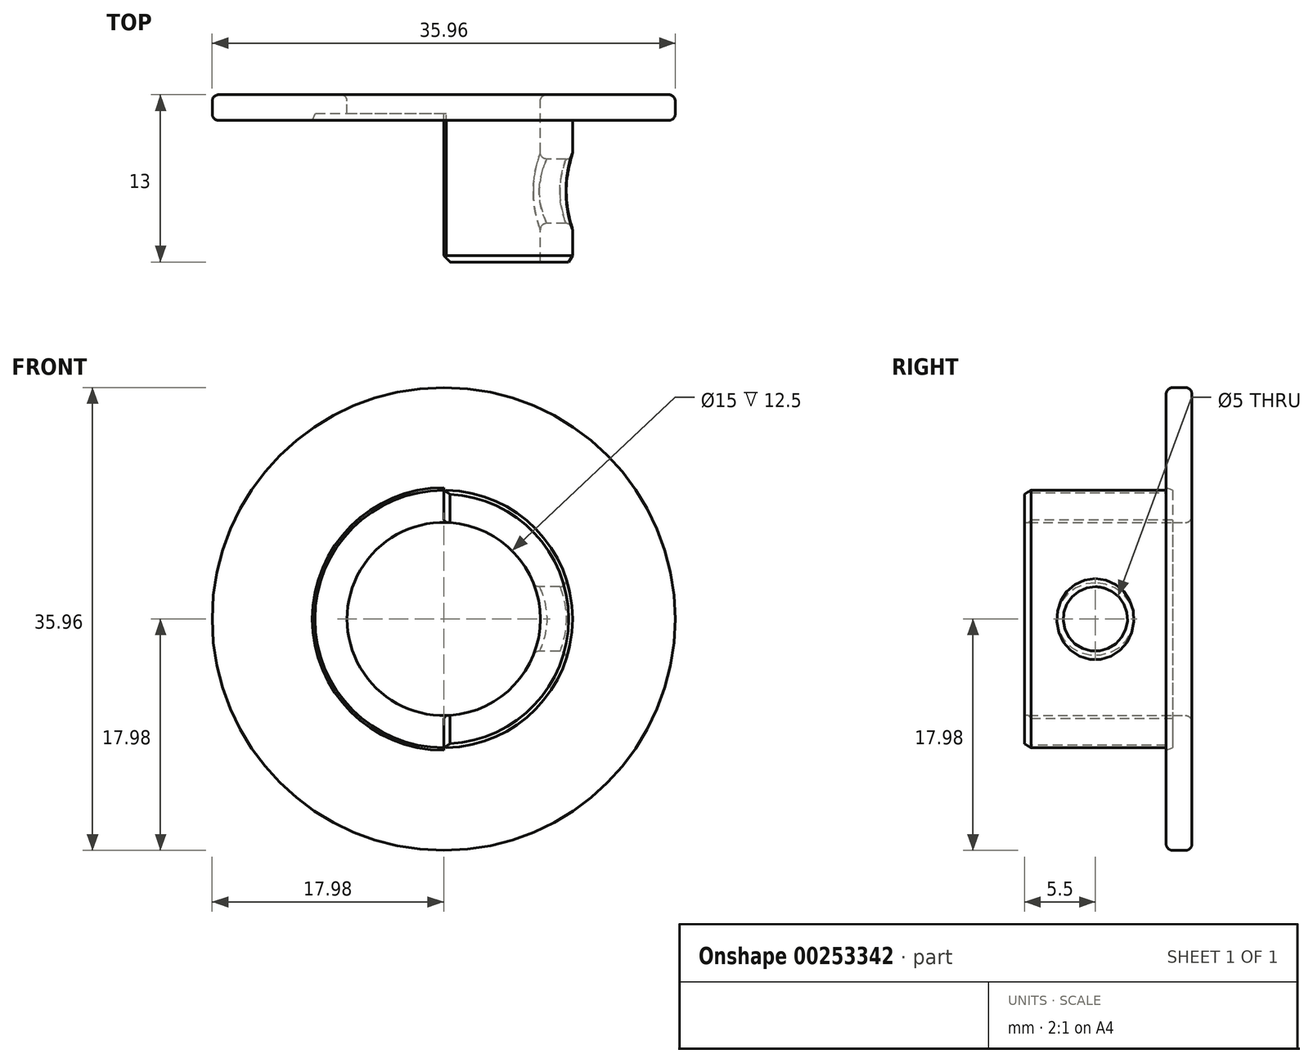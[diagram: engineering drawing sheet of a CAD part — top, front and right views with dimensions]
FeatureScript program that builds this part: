
annotation { "Feature Type Name" : "Feature", "Feature Type Description" : "" }
export const myFeature = defineFeature(function(context is Context, id is Id, definition is map)
    precondition{}
    {
        {
            var Q0;
            Q0=qCreatedBy(makeId("Front.planeOp"),FACE);
            var sketch = newSketch(context, id + "F0", { "sketchPlane" : qUnion([Q0])});
            skCircle(sketch, "E0", {"center": v(0, 0) * mm, "radius": 17.98 * mm});
            skCircle(sketch, "E1", {"center": v(0, 0) * mm, "radius": 10 * mm});
            skCircle(sketch, "E2", {"center": v(0, 0) * mm, "radius": 7.5 * mm});
            skPoint(sketch, "E3", {"position": v(0, 17.98) * mm});
            skLineSegment(sketch, "E4", {"start": v(0, 17.98) * mm, "end": v(0, -17.98) * mm});
            skPoint(sketch, "E5", {"position": v(-17.98, 0) * mm});
            skPoint(sketch, "E6", {"position": v(17.98, 0) * mm});
            skPoint(sketch, "E7", {"position": v(-7.5, 0) * mm});
            skPoint(sketch, "E8", {"position": v(7.5, 0) * mm});
            skSolve(sketch);
        }
        {
            var Q0;
            {var subQ0=sQuery(id+"F0.wireOp",EDGE,"E4");var subQ1=sQuery(id+"F0.wireOp",EDGE,"E0");var subQ2=makeQuery(id+"F0.imprint","INTERSECT",VERTEX,{"disambiguationData":[OD(0.0)],"derivedFrom":[subQ1,subQ0]});Q0=makeQuery(id+"F0.imprint","IMPRINT",FACE,{"disambiguationData":[TD([[makeQuery(id+"F0.imprint","IMPRINT",EDGE,{"disambiguationData":[TD([[subQ2,-1.0]])],"derivedFrom":subQ1}),1.0]])]});}
            var Q1;
            {var subQ0=sQuery(id+"F0.wireOp",EDGE,"E4");var subQ1=sQuery(id+"F0.wireOp",EDGE,"E0");var subQ2=makeQuery(id+"F0.imprint","INTERSECT",VERTEX,{"disambiguationData":[OD(0.0)],"derivedFrom":[subQ1,subQ0]});Q1=makeQuery(id+"F0.imprint","IMPRINT",FACE,{"disambiguationData":[TD([[makeQuery(id+"F0.imprint","IMPRINT",EDGE,{"disambiguationData":[TD([[subQ2,1.0]])],"derivedFrom":subQ1}),1.0]])]});}
            extrude(context, id + "F1", {"entities" : qUnion([Q0, Q1]), "depth" : 2 * mm});
        }
        {
            var Q0;
            {var subQ0=sQuery(id+"F0.wireOp",EDGE,"E4");var subQ1=sQuery(id+"F0.wireOp",EDGE,"E1");var subQ2=makeQuery(id+"F0.imprint","INTERSECT",VERTEX,{"disambiguationData":[OD(0.0)],"derivedFrom":[subQ1,subQ0]});Q0=makeQuery(id+"F0.imprint","IMPRINT",FACE,{"disambiguationData":[TD([[makeQuery(id+"F0.imprint","IMPRINT",EDGE,{"disambiguationData":[TD([[subQ2,-1.0]])],"derivedFrom":subQ1}),1.0]])]});}
            extrude(context, id + "F2", {"entities" : qUnion([Q0]), "operationType" : NewBodyOperationType.ADD, "depth" : 1.5 * mm});
        }
        {
            var Q0;
            {var subQ0=sQuery(id+"F0.wireOp",EDGE,"E4");var subQ1=sQuery(id+"F0.wireOp",EDGE,"E1");var subQ2=makeQuery(id+"F0.imprint","INTERSECT",VERTEX,{"disambiguationData":[OD(0.0)],"derivedFrom":[subQ1,subQ0]});Q0=makeQuery(id+"F0.imprint","IMPRINT",FACE,{"disambiguationData":[TD([[makeQuery(id+"F0.imprint","IMPRINT",EDGE,{"disambiguationData":[TD([[subQ2,1.0]])],"derivedFrom":subQ1}),1.0]])]});}
            extrude(context, id + "F3", {"entities" : qUnion([Q0]), "operationType" : NewBodyOperationType.ADD, "depth" : 13 * mm});
        }
        {
            var Q0;
            Q0=qCreatedBy(makeId("Right.planeOp"),FACE);
            var sketch = newSketch(context, id + "F4", { "sketchPlane" : qUnion([Q0])});
            skCircle(sketch, "E9", {"center": v(-7.5, 0) * mm, "radius": 2.5 * mm});
            skSolve(sketch);
        }
        {
            var Q0;
            Q0=makeQuery(id+"F4.imprint","IMPRINT",FACE,{"disambiguationData":[TD([[makeQuery(id+"F4.imprint","IMPRINT",EDGE,{"derivedFrom":sQuery(id+"F4.wireOp",EDGE,"E9")}),1.0]])]});
            extrude(context, id + "F5", {"entities" : qUnion([Q0]), "operationType" : NewBodyOperationType.REMOVE, "depth" : 25 * mm});
        }
        {
            var Q0;
            Q0=makeQuery(id+"F3.opExtrude","CAP_EDGE",EDGE,{"disambiguationData":[OSD([sQuery(id+"F0.wireOp",EDGE,"E1")])],"isStart":false});
            chamfer(context, id + "F6", {"entities" : qUnion([Q0]), "chamferType" : ChamferType.TWO_OFFSETS, "width1" : 0.3 * mm, "oppositeDirection" : false, "width2" : 0.5 * mm, "tangentPropagation" : true});
        }
        {
            var Q0;
            {var subQ0=sQuery(id+"F0.wireOp",EDGE,"E4");Q0=makeQuery(id+"F3.opExtrude","CAP_EDGE",EDGE,{"disambiguationData":[OSD([subQ0]),TDD([makeQuery(id+"F0.imprint","IMPRINT",EDGE,{"disambiguationData":[TD([[makeQuery(id+"F0.imprint","INTERSECT",VERTEX,{"disambiguationData":[OD(0.0)],"derivedFrom":[sQuery(id+"F0.wireOp",EDGE,"E1"),subQ0]}),-1.0]])],"derivedFrom":subQ0})])],"isStart":false});}
            var Q1;
            {var subQ0=sQuery(id+"F0.wireOp",EDGE,"E4");Q1=makeQuery(id+"F3.opExtrude","CAP_EDGE",EDGE,{"disambiguationData":[OSD([subQ0]),TDD([makeQuery(id+"F0.imprint","IMPRINT",EDGE,{"disambiguationData":[TD([[makeQuery(id+"F0.imprint","INTERSECT",VERTEX,{"disambiguationData":[OD(1.0)],"derivedFrom":[sQuery(id+"F0.wireOp",EDGE,"E1"),subQ0]}),1.0]])],"derivedFrom":subQ0})])],"isStart":false});}
            chamfer(context, id + "F7", {"entities" : qUnion([Q0, Q1]), "width" : 0.5 * mm, "tangentPropagation" : true});
        }
        {
            var Q0;
            Q0=makeQuery(id+"F1.opExtrude","CAP_EDGE",EDGE,{"disambiguationData":[OSD([sQuery(id+"F0.wireOp",EDGE,"E0")])],"isStart":false});
            var Q1;
            Q1=makeQuery(id+"F1.opExtrude","CAP_EDGE",EDGE,{"disambiguationData":[OSD([sQuery(id+"F0.wireOp",EDGE,"E0")])],"isStart":true});
            var Q2;
            {var subQ0=sQuery(id+"F0.wireOp",EDGE,"E2");Q2=makeQuery(id+"F3.boolean.opBoolean","MERGE",EDGE,{"derivedFrom":[makeQuery(id+"F2.opExtrude","CAP_EDGE",EDGE,{"disambiguationData":[OSD([subQ0])],"isStart":true}),makeQuery(id+"F3.opExtrude","CAP_EDGE",EDGE,{"disambiguationData":[OSD([subQ0])],"isStart":true})]});}
            fillet(context, id + "F8", {"entities" : qUnion([Q0, Q1, Q2]), "radius" : 0.5 * mm, "tangentPropagation" : true, "allowEdgeOverflow" : false});
        }
        {
            var Q0;
            {var subQ0=sQuery(id+"F0.wireOp",EDGE,"E2");Q0=makeQuery(id+"F5.boolean.opBoolean","INTERSECT",EDGE,{"derivedFrom":[makeQuery(id+"F3.boolean.opBoolean","MERGE",FACE,{"derivedFrom":[makeQuery(id+"F2.opExtrude","SWEPT_FACE",FACE,{"disambiguationData":[OSD([subQ0])]}),makeQuery(id+"F3.opExtrude","SWEPT_FACE",FACE,{"disambiguationData":[OSD([subQ0])]})]}),makeQuery(id+"F5.opExtrude","SWEPT_FACE",FACE,{"disambiguationData":[OSD([sQuery(id+"F4.wireOp",EDGE,"E9")])]})]});}
            var Q1;
            Q1=makeQuery(id+"F5.boolean.opBoolean","INTERSECT",EDGE,{"derivedFrom":[makeQuery(id+"F3.opExtrude","SWEPT_FACE",FACE,{"disambiguationData":[OSD([sQuery(id+"F0.wireOp",EDGE,"E1")])]}),makeQuery(id+"F5.opExtrude","SWEPT_FACE",FACE,{"disambiguationData":[OSD([sQuery(id+"F4.wireOp",EDGE,"E9")])]})]});
            fillet(context, id + "F9", {"entities" : qUnion([Q0, Q1]), "radius" : 0.5 * mm, "tangentPropagation" : true, "allowEdgeOverflow" : false});
        }
        {
            var Q0;
            {var subQ0=sQuery(id+"F0.wireOp",EDGE,"E1");var subQ1=sQuery(id+"F0.wireOp",EDGE,"E4");var subQ2=makeQuery(id+"F0.imprint","INTERSECT",VERTEX,{"disambiguationData":[OD(0.0)],"derivedFrom":[subQ0,subQ1]});Q0=makeQuery(id+"F3.boolean.opBoolean","SPLIT",EDGE,{"disambiguationData":[topologyDisambiguationEdgeConnected([makeQuery(id+"F3.opExtrude","SWEPT_FACE",FACE,{"disambiguationData":[OSD([subQ0])]})])],"derivedFrom":makeQuery(id+"F3.opExtrude","SWEPT_EDGE",EDGE,{"disambiguationData":[OSD([subQ0,subQ1]),TDD([subQ2])]})});}
            var Q1;
            {var subQ0=sQuery(id+"F0.wireOp",EDGE,"E4");var subQ1=sQuery(id+"F0.wireOp",EDGE,"E2");Q1=makeQuery(id+"F3.opExtrude","SWEPT_EDGE",EDGE,{"disambiguationData":[OSD([subQ1,subQ0]),TDD([makeQuery(id+"F0.imprint","INTERSECT",VERTEX,{"disambiguationData":[OD(0.0)],"derivedFrom":[subQ1,subQ0]})])]});}
            var Q2;
            {var subQ0=sQuery(id+"F0.wireOp",EDGE,"E4");var subQ1=sQuery(id+"F0.wireOp",EDGE,"E2");Q2=makeQuery(id+"F3.opExtrude","SWEPT_EDGE",EDGE,{"disambiguationData":[OSD([subQ1,subQ0]),TDD([makeQuery(id+"F0.imprint","INTERSECT",VERTEX,{"disambiguationData":[OD(1.0)],"derivedFrom":[subQ1,subQ0]})])]});}
            var Q3;
            {var subQ0=sQuery(id+"F0.wireOp",EDGE,"E1");var subQ1=sQuery(id+"F0.wireOp",EDGE,"E4");var subQ2=makeQuery(id+"F0.imprint","INTERSECT",VERTEX,{"disambiguationData":[OD(1.0)],"derivedFrom":[subQ0,subQ1]});Q3=makeQuery(id+"F3.boolean.opBoolean","SPLIT",EDGE,{"disambiguationData":[topologyDisambiguationEdgeConnected([makeQuery(id+"F3.opExtrude","SWEPT_FACE",FACE,{"disambiguationData":[OSD([subQ0])]})])],"derivedFrom":makeQuery(id+"F3.opExtrude","SWEPT_EDGE",EDGE,{"disambiguationData":[OSD([subQ0,subQ1]),TDD([subQ2])]})});}
            chamfer(context, id + "F10", {"entities" : qUnion([Q0, Q1, Q2, Q3]), "width" : 0.2 * mm, "tangentPropagation" : true});
        }
        {
            var Q0;
            {var subQ0=sQuery(id+"F0.wireOp",EDGE,"E1");Q0=makeQuery(id+"F3.boolean.opBoolean","SPLIT",EDGE,{"disambiguationData":[topologyDisambiguationEdgeConnected([makeQuery(id+"F1.opExtrude","SWEPT_FACE",FACE,{"disambiguationData":[OSD([subQ0])]})])],"derivedFrom":makeQuery(id+"F1.opExtrude","CAP_EDGE",EDGE,{"disambiguationData":[OSD([subQ0])],"isStart":false})});}
            chamfer(context, id + "F11", {"entities" : qUnion([Q0]), "chamferType" : ChamferType.TWO_OFFSETS, "width1" : 0.5 * mm, "oppositeDirection" : false, "width2" : 0.2 * mm, "tangentPropagation" : true});
        }
    });
